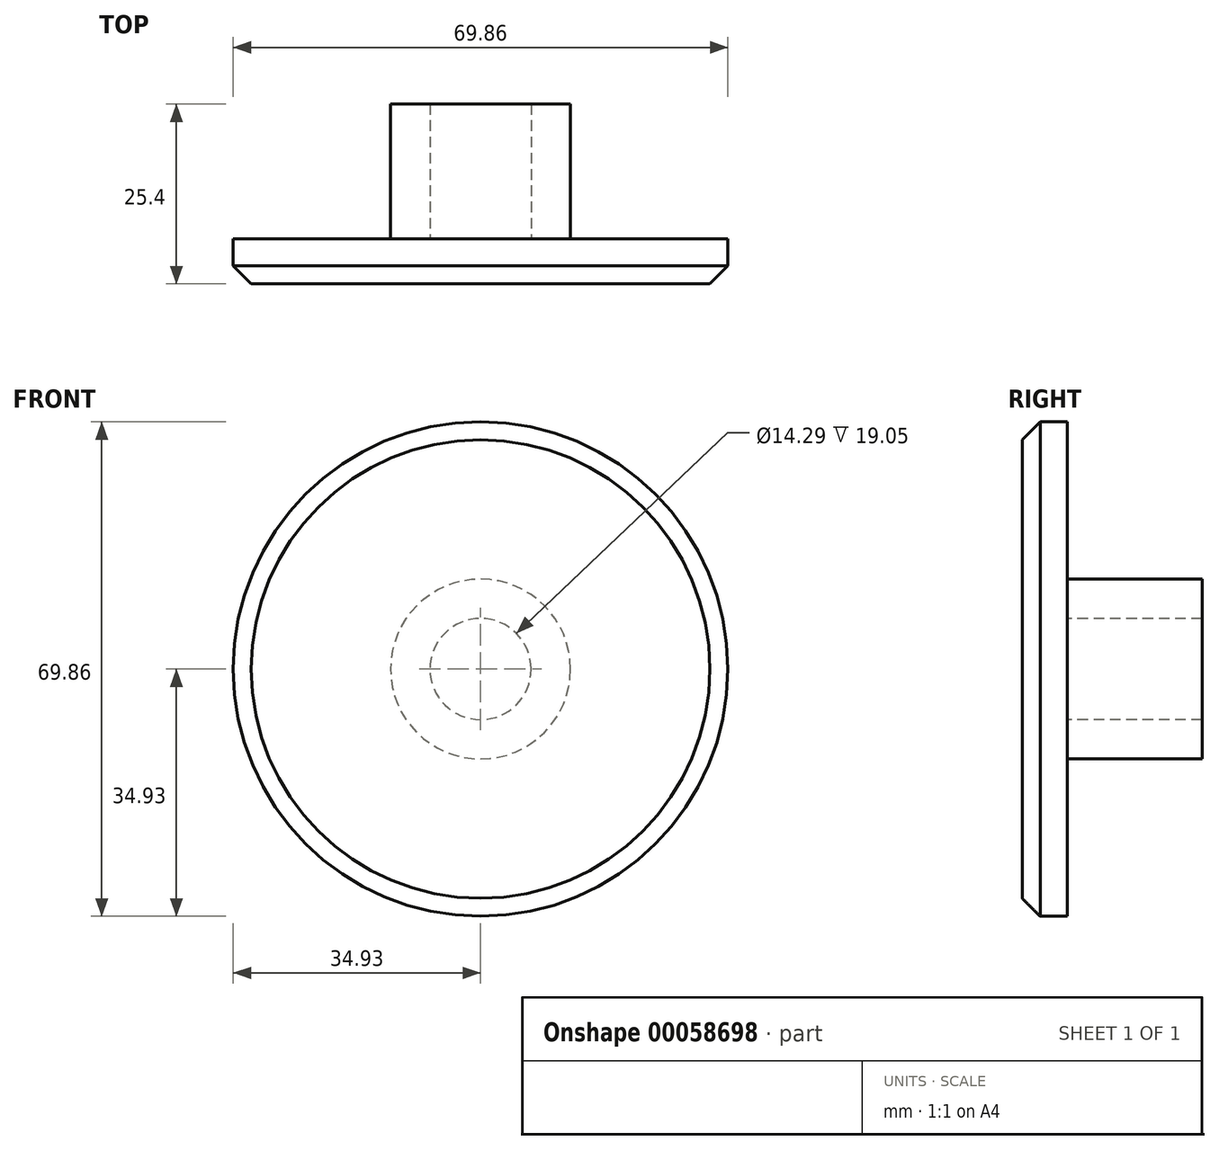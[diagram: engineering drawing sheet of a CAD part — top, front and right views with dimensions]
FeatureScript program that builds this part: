
annotation { "Feature Type Name" : "Feature", "Feature Type Description" : "" }
export const myFeature = defineFeature(function(context is Context, id is Id, definition is map)
    precondition{}
    {
        {
            var Q0;
            Q0=qCreatedBy(makeId("Front.planeOp"),FACE);
            var sketch = newSketch(context, id + "F0", { "sketchPlane" : qUnion([Q0])});
            skCircle(sketch, "E0", {"center": v(0, 0) * mm, "radius": 34.93 * mm});
            skSolve(sketch);
        }
        {
            var Q0;
            Q0=makeQuery(id+"F0.imprint","IMPRINT",FACE,{"disambiguationData":[TD([[makeQuery(id+"F0.imprint","IMPRINT",EDGE,{"derivedFrom":sQuery(id+"F0.wireOp",EDGE,"E0")}),1.0]])]});
            extrude(context, id + "F1", {"entities" : qUnion([Q0]), "depth" : 6.35 * mm});
        }
        {
            var Q0;
            Q0=makeQuery(id+"F1.opExtrude","CAP_FACE",FACE,{"disambiguationData":[OSD([sQuery(id+"F0.wireOp",EDGE,"E0")])],"isStart":false});
            chamfer(context, id + "F2", {"entities" : qUnion([Q0]), "width" : 2.54 * mm, "tangentPropagation" : true});
        }
        {
            var Q0;
            Q0=makeQuery(id+"F1.opExtrude","CAP_FACE",FACE,{"disambiguationData":[OSD([sQuery(id+"F0.wireOp",EDGE,"E0")])],"isStart":true});
            var sketch = newSketch(context, id + "F3", { "sketchPlane" : qUnion([Q0])});
            skCircle(sketch, "E1", {"center": v(0, 0) * mm, "radius": 12.7 * mm});
            skCircle(sketch, "E2", {"center": v(0, 0) * mm, "radius": 7.14 * mm});
            skSolve(sketch);
        }
        {
            var Q0;
            Q0=makeQuery(id+"F3.imprint","IMPRINT",FACE,{"disambiguationData":[TD([[makeQuery(id+"F3.imprint","IMPRINT",EDGE,{"derivedFrom":sQuery(id+"F3.wireOp",EDGE,"E1")}),1.0]])]});
            extrude(context, id + "F4", {"entities" : qUnion([Q0]), "operationType" : NewBodyOperationType.ADD, "depth" : 19.05 * mm});
        }
    });
